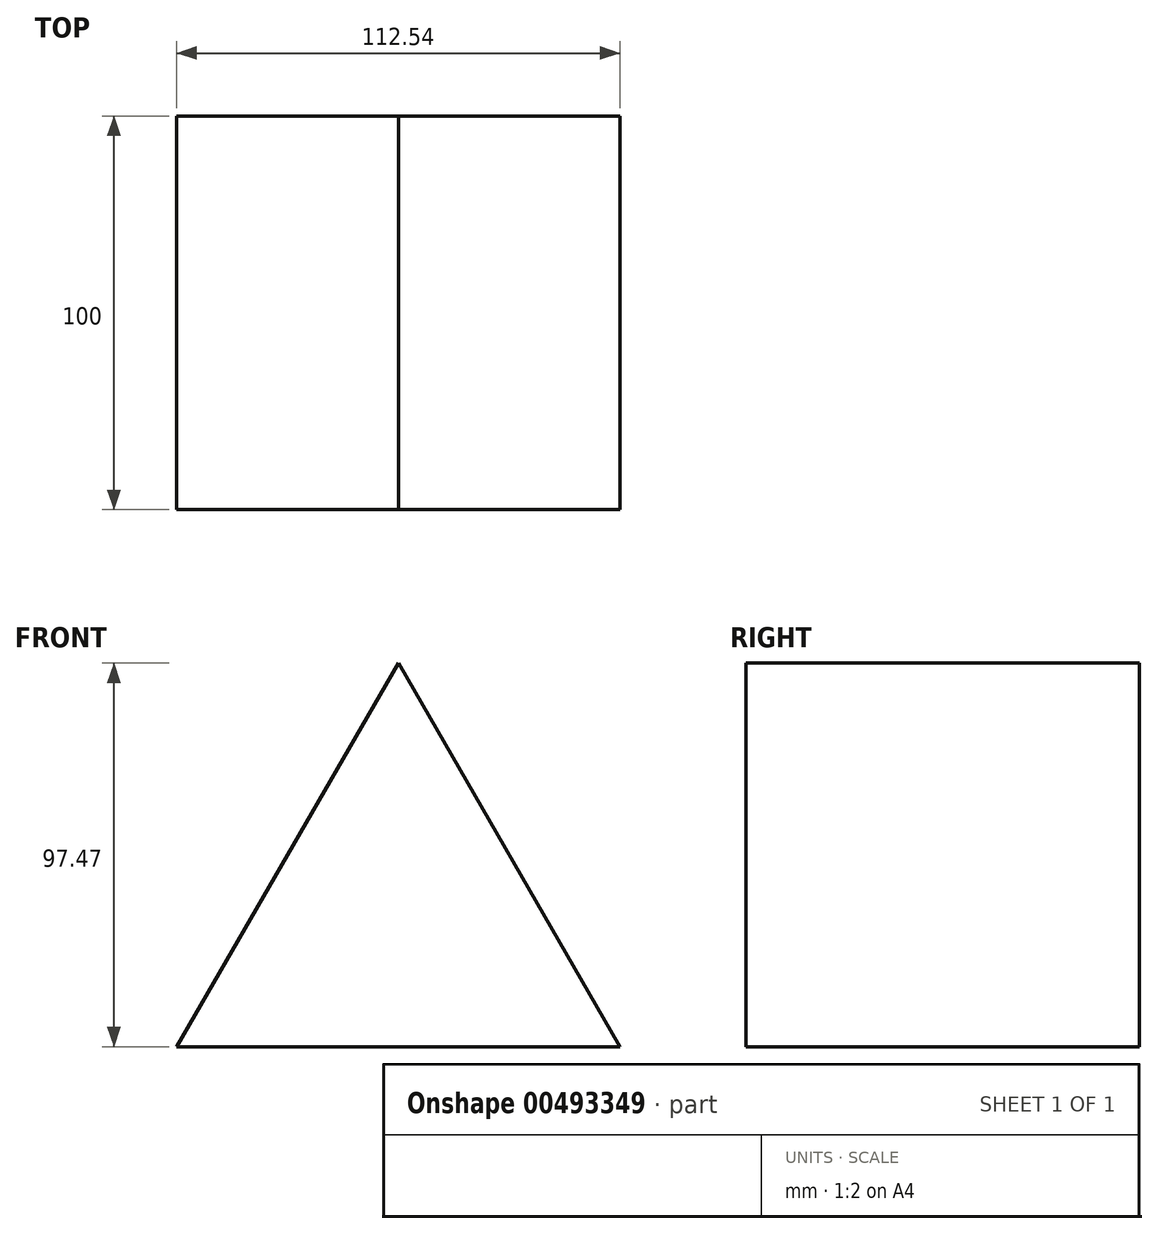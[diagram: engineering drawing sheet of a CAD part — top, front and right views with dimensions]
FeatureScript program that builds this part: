
annotation { "Feature Type Name" : "Feature", "Feature Type Description" : "" }
export const myFeature = defineFeature(function(context is Context, id is Id, definition is map)
    precondition{}
    {
        {
            var Q0;
            Q0=qCreatedBy(makeId("Front.planeOp"),FACE);
            var sketch = newSketch(context, id + "F0", { "sketchPlane" : qUnion([Q0])});
            skCircle(sketch, "E0.cCircle", {"center": v(0, 0) * mm, "radius": 64.98 * mm, "construction": true});
            skLineSegment(sketch, "E0.0", {"start": v(-56.27, -32.49) * mm, "end": v(0, 64.98) * mm});
            skLineSegment(sketch, "E0.1", {"start": v(0, 64.98) * mm, "end": v(56.27, -32.49) * mm});
            skLineSegment(sketch, "E0.2", {"start": v(56.27, -32.49) * mm, "end": v(-56.27, -32.49) * mm});
            skSolve(sketch);
        }
        {
            var Q0;
            Q0 = qSketchRegion(id + "F0", true);
            extrude(context, id + "F1", {"entities" : qUnion([Q0]), "endBound" : BoundingType.SYMMETRIC, "depth" : 100 * mm});
        }
    });
